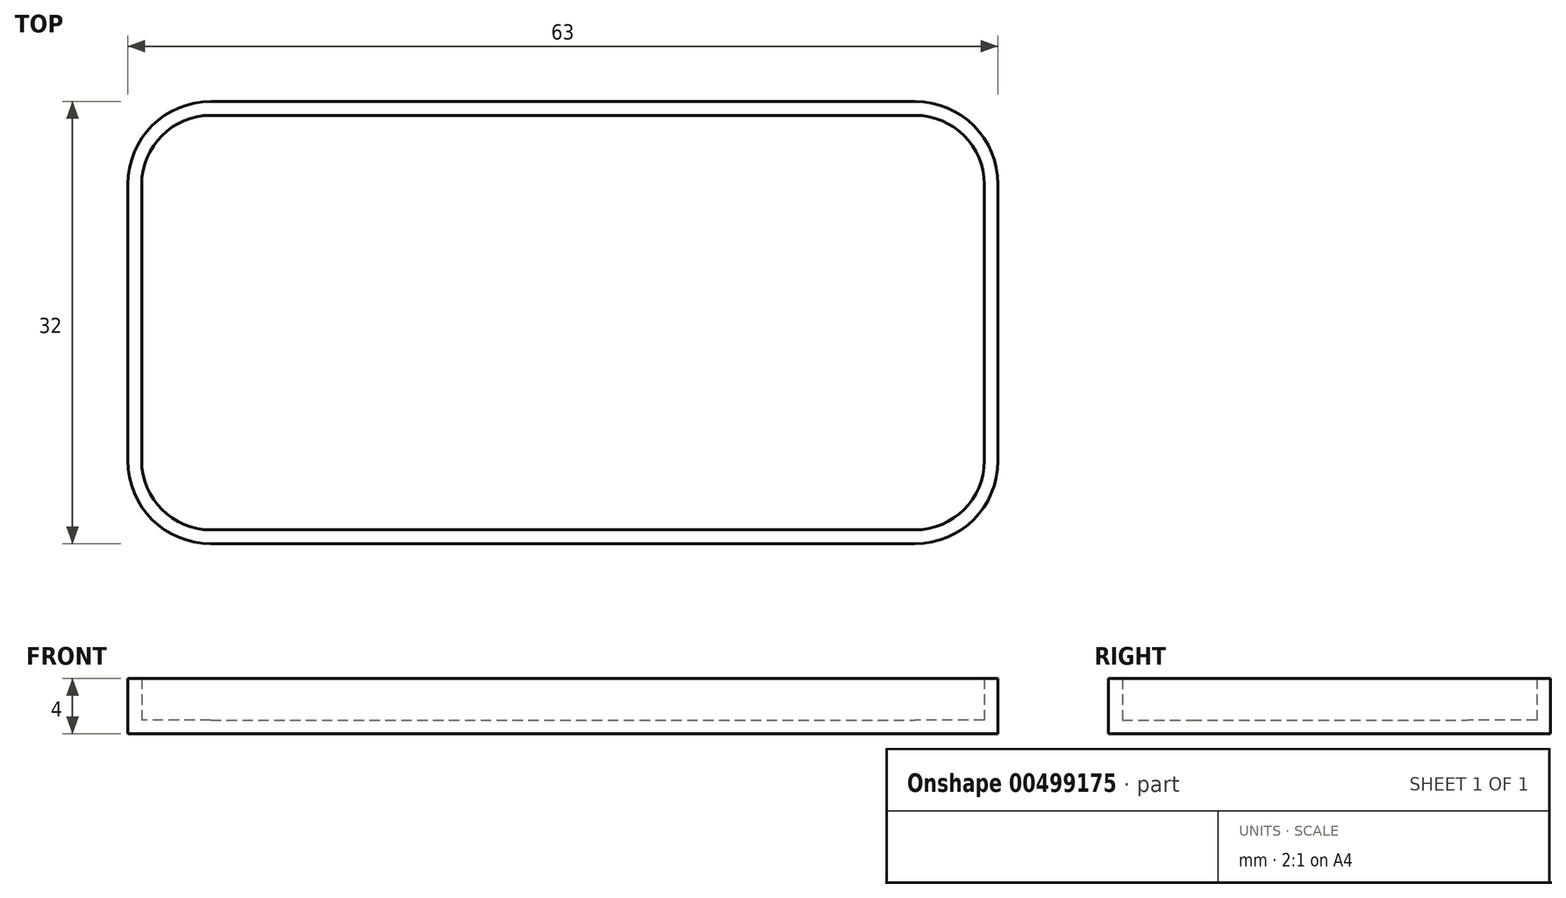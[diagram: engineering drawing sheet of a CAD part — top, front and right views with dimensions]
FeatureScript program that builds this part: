
annotation { "Feature Type Name" : "Feature", "Feature Type Description" : "" }
export const myFeature = defineFeature(function(context is Context, id is Id, definition is map)
    precondition{}
    {
        {
            var Q0;
            Q0=qCreatedBy(makeId("Top.planeOp"),FACE);
            var sketch = newSketch(context, id + "F0", { "sketchPlane" : qUnion([Q0])});
            skLineSegment(sketch, "E0.bottom", {"start": v(5, 0) * mm, "end": v(56, 0) * mm});
            skLineSegment(sketch, "E0.top", {"start": v(5, 30) * mm, "end": v(56, 30) * mm});
            skLineSegment(sketch, "E0.left", {"start": v(0, 5) * mm, "end": v(0, 25) * mm});
            skLineSegment(sketch, "E0.right", {"start": v(61, 5) * mm, "end": v(61, 25) * mm});
            skPoint(sketch, "E1.visualSharp", {"position": v(61, 30) * mm});
            skArc(sketch, "E1.filletArc", {"start": v(61, 25) * mm, "mid": v(59.54, 28.54) * mm, "end": v(56, 30) * mm});
            skPoint(sketch, "E2.visualSharp", {"position": v(0, 30) * mm});
            skArc(sketch, "E2.filletArc", {"start": v(5, 30) * mm, "mid": v(1.46, 28.54) * mm, "end": v(0, 25) * mm});
            skPoint(sketch, "E3.visualSharp", {"position": v(0, 0) * mm});
            skArc(sketch, "E3.filletArc", {"start": v(0, 5) * mm, "mid": v(1.46, 1.46) * mm, "end": v(5, 0) * mm});
            skPoint(sketch, "E4.visualSharp", {"position": v(61, 0) * mm});
            skArc(sketch, "E4.filletArc", {"start": v(56, 0) * mm, "mid": v(59.54, 1.46) * mm, "end": v(61, 5) * mm});
            skLineSegment(sketch, "E5.0", {"start": v(62, 5) * mm, "end": v(62, 25) * mm});
            skArc(sketch, "E6.0", {"start": v(56, -1) * mm, "mid": v(60.24, 0.76) * mm, "end": v(62, 5) * mm});
            skLineSegment(sketch, "E7.0", {"start": v(5, -1) * mm, "end": v(56, -1) * mm});
            skArc(sketch, "E8.0", {"start": v(62, 25) * mm, "mid": v(60.24, 29.24) * mm, "end": v(56, 31) * mm});
            skArc(sketch, "E9.0", {"start": v(5, 31) * mm, "mid": v(0.76, 29.24) * mm, "end": v(-1, 25) * mm});
            skLineSegment(sketch, "E9.1", {"start": v(5, 31) * mm, "end": v(56, 31) * mm});
            skArc(sketch, "E10.0", {"start": v(-1, 5) * mm, "mid": v(0.76, 0.76) * mm, "end": v(5, -1) * mm});
            skLineSegment(sketch, "E10.1", {"start": v(-1, 5) * mm, "end": v(-1, 25) * mm});
            skSolve(sketch);
        }
        {
            var Q0;
            Q0=makeQuery(id+"F0.imprint","IMPRINT",FACE,{"disambiguationData":[TD([[makeQuery(id+"F0.imprint","IMPRINT",EDGE,{"derivedFrom":sQuery(id+"F0.wireOp",EDGE,"E0.bottom")}),1.0]])]});
            extrude(context, id + "F1", {"entities" : qUnion([Q0]), "depth" : 1 * mm, "offsetDistance" : 25 * mm});
        }
        {
            var Q0;
            Q0=makeQuery(id+"F0.imprint","IMPRINT",FACE,{"disambiguationData":[TD([[makeQuery(id+"F0.imprint","IMPRINT",EDGE,{"derivedFrom":sQuery(id+"F0.wireOp",EDGE,"E0.bottom")}),-1.0]])]});
            extrude(context, id + "F2", {"entities" : qUnion([Q0]), "operationType" : NewBodyOperationType.ADD, "depth" : 4 * mm, "offsetDistance" : 25 * mm});
        }
    });
